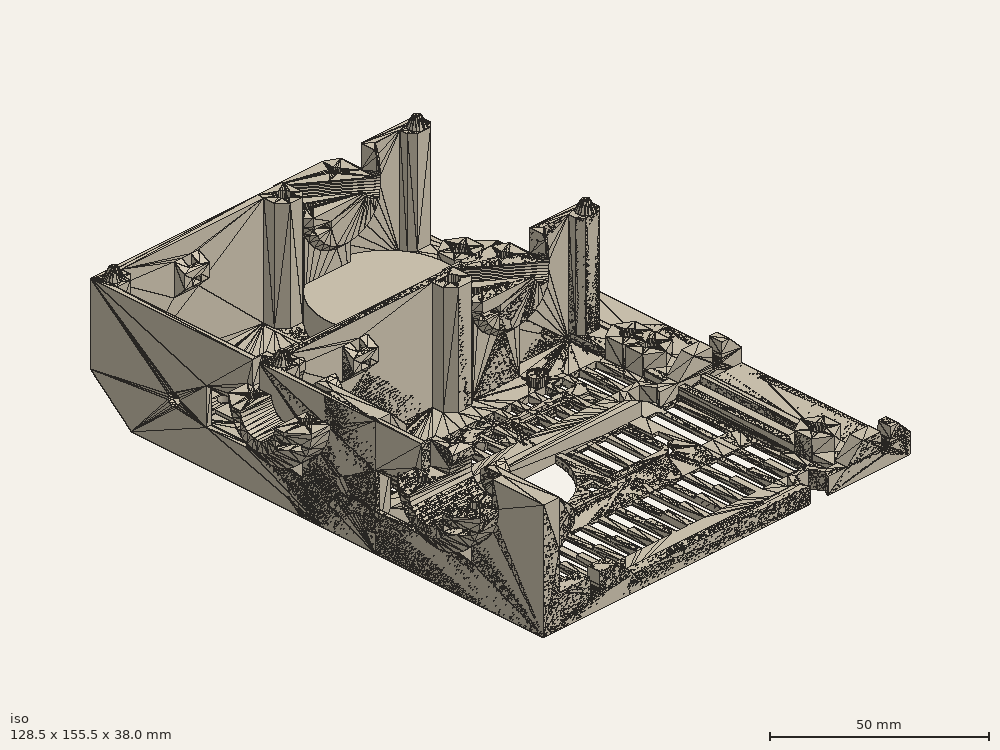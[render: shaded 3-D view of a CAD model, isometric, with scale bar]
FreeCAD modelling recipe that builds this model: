
FCSTD DOCUMENT  (FreeCAD 0.18R14555 (Git shallow))
Label: einsy-box-w-fan
License: All rights reserved
LicenseURL: http://en.wikipedia.org/wiki/All_rights_reserved
objects: Part::Feature×26, Part::Cylinder×25, Part::Box×12, Part::MultiFuse×11, Part::Cut×8, Mesh::Feature×1, Part::Chamfer×1, Part::Fillet×1
note: 84 computed .brp shape members not serialized (recipe doc carries the construction recipe); baked Part::Feature solids carry a one-line shape summary decoded from their .brp

FEATURE [Mesh::Feature] Neat_Habbi_Lappi  label="Neat Habbi-Lappi"
FEATURE [Part::Feature] Neat_Habbi_Lappi001
  shape: bbox 128.5 x 101 x 38 mm, 6798 faces, 0 solids (baked)
FEATURE [Part::Feature] Neat_Habbi_Lappi001_solid  label="Neat_Habbi_Lappi001 (Solid)"
  shape: bbox 128.5 x 101 x 38 mm, 6798 faces (baked)
FEATURE [Part::Box] Box  label="Cube"
  AttacherType = Attacher::AttachEngine3D
  Height = 2
  Length = 42
  Placement = pos=(-1,-1,0) rot=(0,0,1;0rad)
  Width = 42
FEATURE [Part::Cylinder] Cylinder
  Angle = 360
  AttacherType = Attacher::AttachEngine3D
  Height = 10
  Placement = pos=(4,4,0) rot=(0,0,1;0rad)
  Radius = 2
FEATURE [Part::Cylinder] Cylinder001
  Angle = 360
  AttacherType = Attacher::AttachEngine3D
  Height = 10
  Placement = pos=(4,36,0) rot=(0,0,1;0rad)
  Radius = 2
FEATURE [Part::Cylinder] Cylinder002
  Angle = 360
  AttacherType = Attacher::AttachEngine3D
  Height = 10
  Placement = pos=(36,4,0) rot=(0,0,1;0rad)
  Radius = 2
FEATURE [Part::Cylinder] Cylinder003
  Angle = 360
  AttacherType = Attacher::AttachEngine3D
  Height = 10
  Placement = pos=(36,36,0) rot=(0,0,1;0rad)
  Radius = 2
FEATURE [Part::Cylinder] Cylinder004
  Angle = 360
  AttacherType = Attacher::AttachEngine3D
  Height = 2
  Placement = pos=(20,20,0) rot=(0,0,1;0rad)
  Radius = 19
FEATURE [Part::Box] Box001  label="Cube001"
  AttacherType = Attacher::AttachEngine3D
  Height = 2
  Length = 40
  Width = 40
FEATURE [Part::Cylinder] Cylinder005
  Angle = 360
  AttacherType = Attacher::AttachEngine3D
  Height = 2
  Placement = pos=(20,20,0) rot=(0,0,1;0rad)
  Radius = 19
FEATURE [Part::MultiFuse] Fusion
  Shapes = -> [Cylinder004,Cylinder001,Cylinder003,Cylinder002,Cylinder]
FEATURE [Part::Feature] Fusion001
  Placement = pos=(-35,-15,0) rot=(0,0,1;0rad)
  shape: bbox 38 x 38 x 10 mm, 15 faces, 5 solids (baked)
FEATURE [Part::Box] Box002  label="Cube002"
  AttacherType = Attacher::AttachEngine3D
  Height = 2
  Length = 42
  Placement = pos=(-1,-1,0) rot=(0,0,1;0rad)
  Width = 42
FEATURE [Part::Cut] Cut
  Base = -> Box
  Placement = pos=(-29,-15,0) rot=(0,0,1;0rad)
  Tool = -> Fusion
FEATURE [Part::Chamfer] Chamfer
  Base = -> Cut
  Edges = 4 edges r=2: [Edge1,Edge3,Edge6,Edge16]
  Placement = pos=(-6,0,0) rot=(0,0,1;0rad)
FEATURE [Part::Cut] Cut001
  Base = -> Neat_Habbi_Lappi001_solid
  Tool = -> Fusion001
FEATURE [Part::MultiFuse] Fusion002
  Shapes = -> [Chamfer,Cut001]
FEATURE [Part::Feature] Fusion002_solid  label="Fusion002 (Solid)"
  shape: bbox 128.5 x 101 x 38 mm, 6664 faces (baked)
FEATURE [Part::Box] Box003  label="Cube003"
  AttacherType = Attacher::AttachEngine3D
  Height = 2
  Length = 40
  Width = 40
FEATURE [Part::Cylinder] Cylinder006
  Angle = 360
  AttacherType = Attacher::AttachEngine3D
  Height = 10
  Placement = pos=(4,4,0) rot=(0,0,1;0rad)
  Radius = 1.6
FEATURE [Part::Cylinder] Cylinder007
  Angle = 360
  AttacherType = Attacher::AttachEngine3D
  Height = 10
  Placement = pos=(36,4,0) rot=(0,0,1;0rad)
  Radius = 1.6
FEATURE [Part::Cylinder] Cylinder008
  Angle = 360
  AttacherType = Attacher::AttachEngine3D
  Height = 10
  Placement = pos=(4,36,0) rot=(0,0,1;0rad)
  Radius = 1.6
FEATURE [Part::Cylinder] Cylinder009
  Angle = 360
  AttacherType = Attacher::AttachEngine3D
  Height = 10
  Placement = pos=(36,36,0) rot=(0,0,1;0rad)
  Radius = 1.6
FEATURE [Part::Feature] Body001
  Placement = pos=(5,20,0) rot=(0,0,1;0rad)
  shape: bbox 8.66 x 10 x 2 mm, 8 faces (baked)
FEATURE [Part::Feature] Body002
  Placement = pos=(35,20,0) rot=(0,0,1;0rad)
  shape: bbox 8.66 x 10 x 2 mm, 8 faces (baked)
FEATURE [Part::Feature] Body003
  Placement = pos=(25,20,0) rot=(0,0,1;0rad)
  shape: bbox 8.66 x 10 x 2 mm, 8 faces (baked)
FEATURE [Part::Feature] Body004
  Placement = pos=(15,20,0) rot=(0,0,1;0rad)
  shape: bbox 8.66 x 10 x 2 mm, 8 faces (baked)
FEATURE [Part::Feature] Body005
  Placement = pos=(10,29,0) rot=(0,0,1;0rad)
  shape: bbox 8.66 x 10 x 2 mm, 8 faces (baked)
FEATURE [Part::Feature] Body006
  Placement = pos=(10,11,0) rot=(0,0,1;0rad)
  shape: bbox 8.66 x 10 x 2 mm, 8 faces (baked)
FEATURE [Part::Feature] Body007
  Placement = pos=(20,29,0) rot=(0,0,1;0rad)
  shape: bbox 8.66 x 10 x 2 mm, 8 faces (baked)
FEATURE [Part::Feature] Body008
  Placement = pos=(20,11,0) rot=(0,0,1;0rad)
  shape: bbox 8.66 x 10 x 2 mm, 8 faces (baked)
FEATURE [Part::Feature] Body009
  Placement = pos=(30,11,0) rot=(0,0,1;0rad)
  shape: bbox 8.66 x 10 x 2 mm, 8 faces (baked)
FEATURE [Part::Feature] Body010
  Placement = pos=(30,29,0) rot=(0,0,1;0rad)
  shape: bbox 8.66 x 10 x 2 mm, 8 faces (baked)
FEATURE [Part::Feature] Body011
  Placement = pos=(25,38,0) rot=(0,0,1;0rad)
  shape: bbox 8.66 x 10 x 2 mm, 8 faces (baked)
FEATURE [Part::Feature] Body012
  Placement = pos=(15,38,0) rot=(0,0,1;0rad)
  shape: bbox 8.66 x 10 x 2 mm, 8 faces (baked)
FEATURE [Part::Feature] Body013
  Placement = pos=(15,2,0) rot=(0,0,1;0rad)
  shape: bbox 8.66 x 10 x 2 mm, 8 faces (baked)
FEATURE [Part::Feature] Body014
  Placement = pos=(25,2,0) rot=(0,0,1;0rad)
  shape: bbox 8.66 x 10 x 2 mm, 8 faces (baked)
FEATURE [Part::Cylinder] Cylinder010
  Angle = 360
  AttacherType = Attacher::AttachEngine3D
  Height = 10
  Placement = pos=(20,20,0) rot=(0,0,1;0rad)
  Radius = 19
FEATURE [Part::Feature] Body015
  Placement = pos=(40,11,0) rot=(0,0,1;0rad)
  shape: bbox 8.66 x 10 x 2 mm, 8 faces (baked)
FEATURE [Part::Feature] Body016
  Placement = pos=(0,11,0) rot=(0,0,1;0rad)
  shape: bbox 8.66 x 10 x 2 mm, 8 faces (baked)
FEATURE [Part::Feature] Body021
  Placement = pos=(0,29,0) rot=(0,0,1;0rad)
  shape: bbox 8.66 x 10 x 2 mm, 8 faces (baked)
FEATURE [Part::Feature] Body022
  Placement = pos=(40,29,0) rot=(0,0,1;0rad)
  shape: bbox 8.66 x 10 x 2 mm, 8 faces (baked)
FEATURE [Part::Box] Box004  label="Cube004"
  AttacherType = Attacher::AttachEngine3D
  Height = 10
  Length = 40
  Placement = pos=(0,-4,0) rot=(0,0,1;0rad)
  Width = 6
FEATURE [Part::MultiFuse] Fusion004
  Shapes = -> [Body015,Body011,Body012,Body022,Body013,Body003,Body010,Body014,Body001,Body008,Body009,Body007,Body016,Body005,Body021,Body004,Body006,Body002]
FEATURE [Part::Box] Box005  label="Cube005"
  AttacherType = Attacher::AttachEngine3D
  Height = 10
  Length = 40
  Placement = pos=(0,38,0) rot=(0,0,1;0rad)
  Width = 6
FEATURE [Part::Box] Box006  label="Cube006"
  AttacherType = Attacher::AttachEngine3D
  Height = 10
  Length = 10
  Placement = pos=(-8,0,0) rot=(0,0,1;0rad)
  Width = 40
FEATURE [Part::Box] Box007  label="Cube007"
  AttacherType = Attacher::AttachEngine3D
  Height = 10
  Length = 10
  Placement = pos=(38,0,0) rot=(0,0,1;0rad)
  Width = 40
FEATURE [Part::MultiFuse] Fusion005
  Shapes = -> [Box005,Box006,Box007,Box004]
FEATURE [Part::Cut] Cut003
  Base = -> Fusion004
  Tool = -> Fusion005
FEATURE [Part::Cylinder] Cylinder011
  Angle = 360
  AttacherType = Attacher::AttachEngine3D
  Height = 1
  Placement = pos=(4,4,1.5) rot=(0,0,1;0rad)
  Radius = 3.1
FEATURE [Part::MultiFuse] Fusion006
  Shapes = -> [Cylinder006,Cylinder009,Cylinder008,Cylinder007]
FEATURE [Part::Cut] Cut004
  Base = -> Box003
  Tool = -> Fusion006
FEATURE [Part::Cylinder] Cylinder012
  Angle = 360
  AttacherType = Attacher::AttachEngine3D
  Height = 1
  Placement = pos=(36,4,1.5) rot=(0,0,1;0rad)
  Radius = 3.1
FEATURE [Part::Cylinder] Cylinder013
  Angle = 360
  AttacherType = Attacher::AttachEngine3D
  Height = 1
  Placement = pos=(4,36,1.5) rot=(0,0,1;0rad)
  Radius = 3.1
FEATURE [Part::Cylinder] Cylinder014
  Angle = 360
  AttacherType = Attacher::AttachEngine3D
  Height = 1
  Placement = pos=(36,36,1.5) rot=(0,0,1;0rad)
  Radius = 3.1
FEATURE [Part::Cylinder] Cylinder015
  Angle = 360
  AttacherType = Attacher::AttachEngine3D
  Height = 2
  Placement = pos=(1,-11,0) rot=(0,0,1;0rad)
  Radius = 3
FEATURE [Part::Cylinder] Cylinder016
  Angle = 360
  AttacherType = Attacher::AttachEngine3D
  Height = 2
  Placement = pos=(-31,-11,0) rot=(0,0,1;0rad)
  Radius = 3
FEATURE [Part::Cylinder] Cylinder017
  Angle = 360
  AttacherType = Attacher::AttachEngine3D
  Height = 2
  Placement = pos=(1,21,0) rot=(0,0,1;0rad)
  Radius = 3
FEATURE [Part::Cylinder] Cylinder018
  Angle = 360
  AttacherType = Attacher::AttachEngine3D
  Height = 2
  Placement = pos=(-31,21,0) rot=(0,0,1;0rad)
  Radius = 3
FEATURE [Part::Cylinder] Cylinder019
  Angle = 360
  AttacherType = Attacher::AttachEngine3D
  Height = 2
  Placement = pos=(-31,21,0) rot=(0,0,1;0rad)
  Radius = 1.6
FEATURE [Part::Cylinder] Cylinder020
  Angle = 360
  AttacherType = Attacher::AttachEngine3D
  Height = 2
  Placement = pos=(1,-11,0) rot=(0,0,1;0rad)
  Radius = 1.6
FEATURE [Part::Cylinder] Cylinder021
  Angle = 360
  AttacherType = Attacher::AttachEngine3D
  Height = 2
  Placement = pos=(-31,-11,0) rot=(0,0,1;0rad)
  Radius = 1.6
FEATURE [Part::Cylinder] Cylinder022
  Angle = 360
  AttacherType = Attacher::AttachEngine3D
  Height = 2
  Placement = pos=(1,21,0) rot=(0,0,1;0rad)
  Radius = 1.6
FEATURE [Part::MultiFuse] Fusion008
  Shapes = -> [Cylinder018,Cylinder015,Cylinder016,Cylinder017,Fusion002]
FEATURE [Part::MultiFuse] Fusion009
  Shapes = -> [Cylinder022,Cylinder019,Cylinder020,Cylinder021]
FEATURE [Part::Cut] Cut007
  Base = -> Fusion008
  Tool = -> Fusion009
FEATURE [Part::Box] Box008  label="Cube008"
  AttacherType = Attacher::AttachEngine3D
  Height = 1
  Length = 5.5
  Placement = pos=(-1.75,-13.75,1) rot=(0,0,1;0rad)
  Width = 5.5
FEATURE [Part::Box] Box009  label="Cube009"
  AttacherType = Attacher::AttachEngine3D
  Height = 1
  Length = 5.5
  Placement = pos=(-1.75,18.25,1) rot=(0,0,1;0rad)
  Width = 5.5
FEATURE [Part::Box] Box010  label="Cube010"
  AttacherType = Attacher::AttachEngine3D
  Height = 1
  Length = 5.5
  Placement = pos=(-33.75,-13.75,1) rot=(0,0,1;0rad)
  Width = 5.5
FEATURE [Part::Box] Box011  label="Cube011"
  AttacherType = Attacher::AttachEngine3D
  Height = 1
  Length = 5.5
  Placement = pos=(-33.75,18.25,1) rot=(0,0,1;0rad)
  Width = 5.5
FEATURE [Part::MultiFuse] Fusion010
  Shapes = -> [Box011,Box008,Box009,Box010]
FEATURE [Part::Cut] Cut008
  Base = -> Cut007
  Placement = pos=(0,-54.5,0) rot=(0,0,1;0rad)
  Tool = -> Fusion010
FEATURE [Part::MultiFuse] Fusion011
  Placement = pos=(0,0,-0.5) rot=(0,0,1;0rad)
  Shapes = -> [Cylinder012,Cylinder013,Cylinder011,Cylinder014]
FEATURE [Part::MultiFuse] Fusion012
  Shapes = -> [Cut003,Fusion011]
FEATURE [Part::Cut] Cut009
  Base = -> Cut004
  Tool = -> Fusion012
FEATURE [Part::Fillet] Fillet  label="fan-guard"
  Base = -> Cut009
  Edges = 4 edges r=2: [Edge1,Edge3,Edge6,Edge111]
FEATURE [Part::Cylinder] Cylinder023
  Angle = 360
  AttacherType = Attacher::AttachEngine3D
  Height = 81
  Placement = pos=(-56.95,-68.5,0) rot=(0,0,1;0rad)
  Radius = 1.6
FEATURE [Part::Cylinder] Cylinder024
  Angle = 360
  AttacherType = Attacher::AttachEngine3D
  Height = 81
  Placement = pos=(-56.95,-85.5,0) rot=(0,0,1;0rad)
  Radius = 1.6
FEATURE [Part::MultiFuse] Fusion013
  Shapes = -> [Cylinder023,Cylinder024]
FEATURE [Part::Cut] Cut010  label="base"
  Base = -> Cut008
  Tool = -> Fusion013
FEATURE [Part::Feature] Cut010001  label="Cut011"
  shape: bbox 128.5 x 101 x 38 mm, 2506 faces (baked)
FEATURE [Part::Feature] Cut010001_solid  label="Cut011 (Solid)"
  shape: bbox 128.5 x 101 x 38 mm, 2506 faces (baked)
FEATURE [Part::Feature] Fillet001  label="fan-guard001"
  shape: bbox 40 x 40 x 2 mm, 118 faces (baked)
FEATURE [Part::Feature] Fillet001_solid  label="fan-guard001 (Solid)"
  shape: bbox 40 x 40 x 2 mm, 118 faces (baked)
